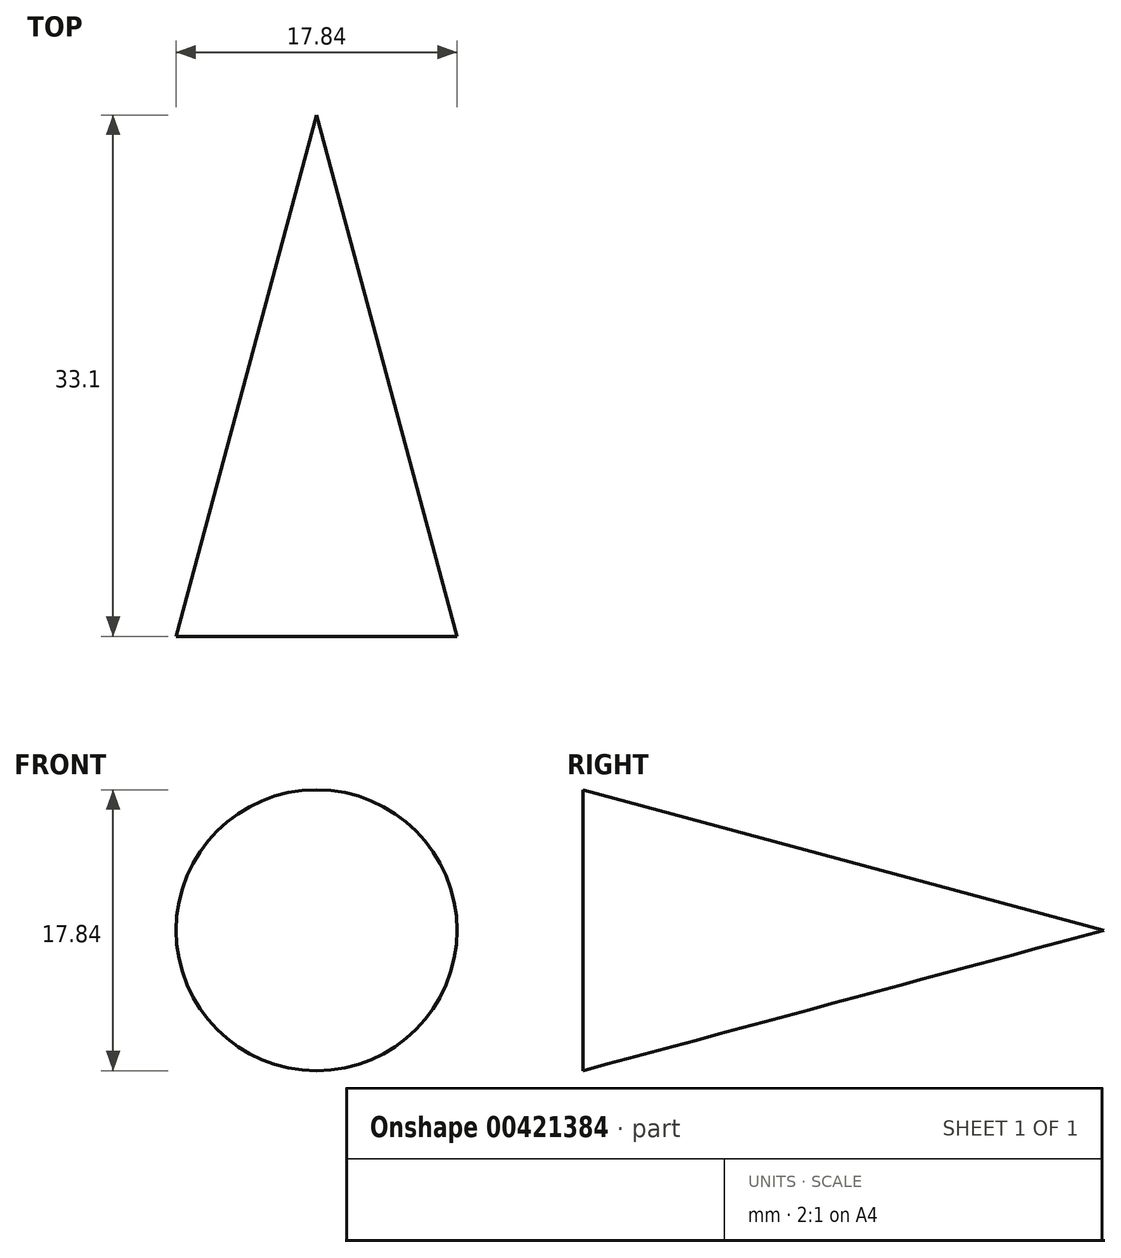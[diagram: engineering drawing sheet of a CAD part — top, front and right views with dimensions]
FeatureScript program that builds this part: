
annotation { "Feature Type Name" : "Feature", "Feature Type Description" : "" }
export const myFeature = defineFeature(function(context is Context, id is Id, definition is map)
    precondition{}
    {
        {
            var Q0;
            Q0=qCreatedBy(makeId("Top.planeOp"),FACE);
            var sketch = newSketch(context, id + "F0", { "sketchPlane" : qUnion([Q0])});
            skLineSegment(sketch, "E0", {"start": v(0, 0) * mm, "end": v(0, 33.1) * mm});
            skLineSegment(sketch, "E1", {"start": v(0, 33.1) * mm, "end": v(8.92, 0) * mm});
            skLineSegment(sketch, "E2", {"start": v(8.92, 0) * mm, "end": v(0, 0) * mm});
            skSolve(sketch);
        }
        {
            var Q0;
            Q0 = qSketchRegion(id + "F0", true);
            var Q1;
            Q1=sQuery(id+"F0.wireOp",EDGE,"E0");
            revolve(context, id + "F1", {"entities" : qUnion([Q0]), "axis" : qUnion([Q1]), "revolveType" : RevolveType.FULL});
        }
    });
